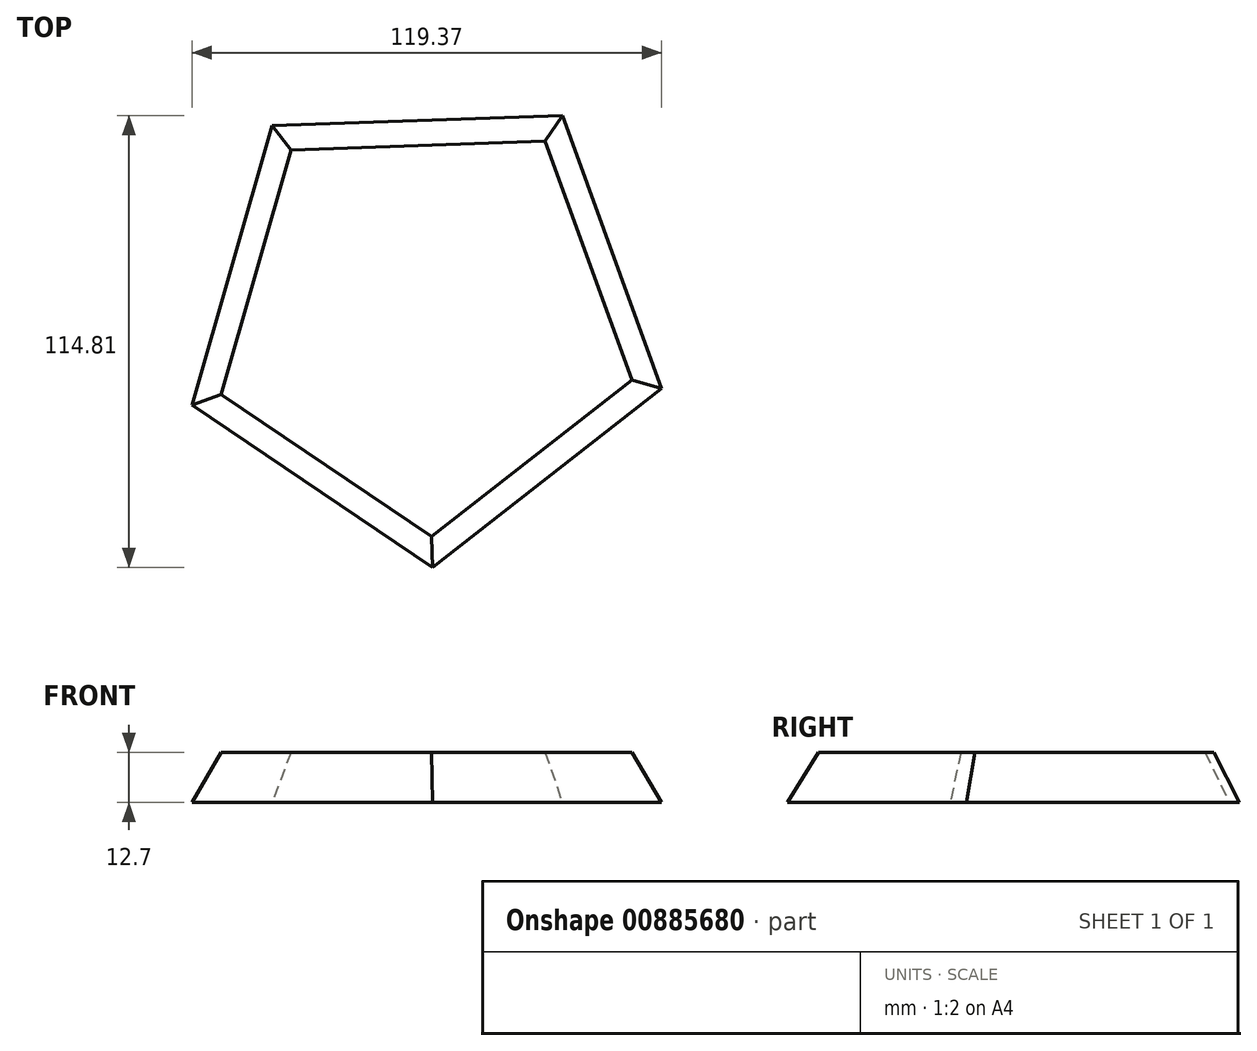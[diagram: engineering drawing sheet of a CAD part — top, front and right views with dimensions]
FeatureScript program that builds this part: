
annotation { "Feature Type Name" : "Feature", "Feature Type Description" : "" }
export const myFeature = defineFeature(function(context is Context, id is Id, definition is map)
    precondition{}
    {
        {
            var Q0;
            Q0=qCreatedBy(makeId("Top.planeOp"),FACE);
            var sketch = newSketch(context, id + "F0", { "sketchPlane" : qUnion([Q0])});
            skCircle(sketch, "E0.cCircle", {"center": v(0, 0) * mm, "radius": 50.8 * mm, "construction": true});
            skLineSegment(sketch, "E0.0", {"start": v(-38.66, 49.48) * mm, "end": v(35.11, 52.06) * mm});
            skLineSegment(sketch, "E0.1", {"start": v(35.11, 52.06) * mm, "end": v(60.36, -17.3) * mm});
            skLineSegment(sketch, "E0.2", {"start": v(60.36, -17.3) * mm, "end": v(2.2, -62.75) * mm});
            skLineSegment(sketch, "E0.3", {"start": v(2.2, -62.75) * mm, "end": v(-59, -21.48) * mm});
            skLineSegment(sketch, "E0.4", {"start": v(-59, -21.48) * mm, "end": v(-38.66, 49.48) * mm});
            skPoint(sketch, "E0.0.midPoint", {"position": v(-1.77, 50.77) * mm});
            skSolve(sketch);
        }
        {
            var Q0;
            Q0=qCreatedBy(makeId("Top.planeOp"),FACE);
            cPlane(context, id + "F1", {"entities" : qUnion([Q0]), "cplaneType" : CPlaneType.OFFSET, "offset" : 12.7 * mm, "width" : 152.4 * mm, "height" : 152.4 * mm});
        }
        {
            var Q0;
            Q0=qCreatedBy(id+"F1.planeOp",FACE);
            var sketch = newSketch(context, id + "F2", { "sketchPlane" : qUnion([Q0])});
            skCircle(sketch, "E1.cCircle", {"center": v(0, 0) * mm, "radius": 44.44 * mm, "construction": true});
            skLineSegment(sketch, "E1.0", {"start": v(-51.62, -18.79) * mm, "end": v(-33.82, 43.29) * mm});
            skLineSegment(sketch, "E1.1", {"start": v(-33.82, 43.29) * mm, "end": v(30.72, 45.54) * mm});
            skLineSegment(sketch, "E1.2", {"start": v(30.72, 45.54) * mm, "end": v(52.8, -15.14) * mm});
            skLineSegment(sketch, "E1.3", {"start": v(52.8, -15.14) * mm, "end": v(1.92, -54.9) * mm});
            skLineSegment(sketch, "E1.4", {"start": v(1.92, -54.9) * mm, "end": v(-51.62, -18.79) * mm});
            skPoint(sketch, "E1.0.midPoint", {"position": v(-42.72, 12.25) * mm});
            skSolve(sketch);
        }
        {
            var Q0;
            Q0=makeQuery(id+"F2.imprint","IMPRINT",FACE,{"disambiguationData":[TD([[makeQuery(id+"F2.imprint","IMPRINT",EDGE,{"derivedFrom":sQuery(id+"F2.wireOp",EDGE,"E1.0")}),-1.0]])]});
            var Q1;
            Q1=makeQuery(id+"F0.imprint","IMPRINT",FACE,{"disambiguationData":[TD([[makeQuery(id+"F0.imprint","IMPRINT",EDGE,{"derivedFrom":sQuery(id+"F0.wireOp",EDGE,"E0.0")}),-1.0]])]});
            loft(context, id + "F3", {"sheetProfilesArray" : [{ "sheetProfileEntities" : qUnion([Q0]) }, { "sheetProfileEntities" : qUnion([Q1]) }]});
        }
    });
